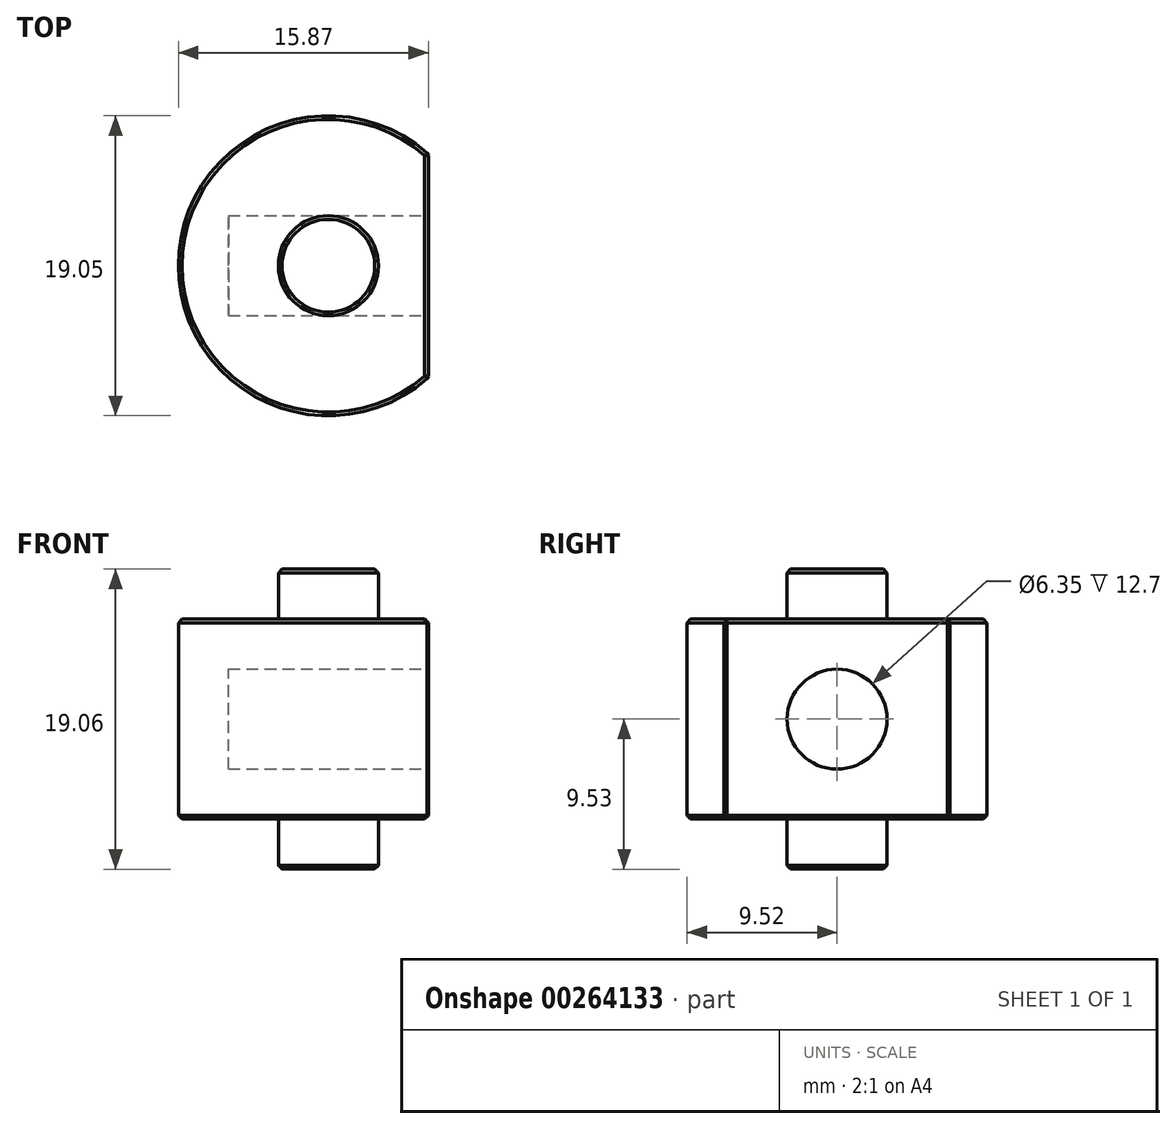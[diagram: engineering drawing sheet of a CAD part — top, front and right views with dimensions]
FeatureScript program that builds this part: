
annotation { "Feature Type Name" : "Feature", "Feature Type Description" : "" }
export const myFeature = defineFeature(function(context is Context, id is Id, definition is map)
    precondition{}
    {
        {
            var Q0;
            Q0=qCreatedBy(makeId("Top.planeOp"),FACE);
            var sketch = newSketch(context, id + "F0", { "sketchPlane" : qUnion([Q0])});
            skCircle(sketch, "E0", {"center": v(0, 0) * mm, "radius": 9.53 * mm});
            skLineSegment(sketch, "E1", {"start": v(6.35, 7.1) * mm, "end": v(6.35, -7.1) * mm});
            skSolve(sketch);
        }
        {
            var Q0;
            {var subQ0=sQuery(id+"F0.wireOp",EDGE,"E1");Q0=makeQuery(id+"F0.imprint","IMPRINT",FACE,{"disambiguationData":[TD([[makeQuery(id+"F0.imprint","IMPRINT",EDGE,{"derivedFrom":subQ0}),-1.0]])]});}
            extrude(context, id + "F1", {"entities" : qUnion([Q0]), "depth" : 12.7 * mm});
        }
        {
            var Q0;
            Q0=makeQuery(id+"F1.opExtrude","CAP_FACE",FACE,{"disambiguationData":[OSD([sQuery(id+"F0.wireOp",EDGE,"E0")])],"isStart":false});
            var sketch = newSketch(context, id + "F2", { "sketchPlane" : qUnion([Q0])});
            skCircle(sketch, "E2", {"center": v(0, 0) * mm, "radius": 3.18 * mm});
            skSolve(sketch);
        }
        {
            var Q0;
            Q0 = qSketchRegion(id + "F2", true);
            extrude(context, id + "F3", {"entities" : qUnion([Q0]), "operationType" : NewBodyOperationType.ADD, "depth" : 3.17 * mm});
        }
        {
            var Q0;
            Q0=makeQuery(id+"F1.opExtrude","CAP_FACE",FACE,{"disambiguationData":[OSD([sQuery(id+"F0.wireOp",EDGE,"E0")])],"isStart":true});
            var sketch = newSketch(context, id + "F4", { "sketchPlane" : qUnion([Q0])});
            skCircle(sketch, "E3", {"center": v(0, 0) * mm, "radius": 3.18 * mm});
            skSolve(sketch);
        }
        {
            var Q0;
            Q0 = qSketchRegion(id + "F4", true);
            extrude(context, id + "F5", {"entities" : qUnion([Q0]), "operationType" : NewBodyOperationType.ADD, "depth" : 3.17 * mm});
        }
        {
            var Q0;
            Q0=makeQuery(id+"F3.opExtrude","CAP_EDGE",EDGE,{"disambiguationData":[OSD([sQuery(id+"F2.wireOp",EDGE,"E2")])],"isStart":false});
            var Q1;
            Q1=makeQuery(id+"F1.opExtrude","CAP_EDGE",EDGE,{"disambiguationData":[OSD([sQuery(id+"F0.wireOp",EDGE,"E0")])],"isStart":false});
            var Q2;
            Q2=makeQuery(id+"F1.opExtrude","CAP_EDGE",EDGE,{"disambiguationData":[OSD([sQuery(id+"F0.wireOp",EDGE,"E1")])],"isStart":false});
            var Q3;
            {var subQ0=sQuery(id+"F0.wireOp",EDGE,"E1");var subQ1=sQuery(id+"F0.wireOp",EDGE,"E0");Q3=makeQuery(id+"F1.opExtrude","SWEPT_EDGE",EDGE,{"disambiguationData":[OSD([subQ1,subQ0]),TDD([makeQuery(id+"F0.imprint","INTERSECT",VERTEX,{"disambiguationData":[OD(0.0)],"derivedFrom":[subQ1,subQ0]})])]});}
            var Q4;
            Q4=makeQuery(id+"F1.opExtrude","CAP_EDGE",EDGE,{"disambiguationData":[OSD([sQuery(id+"F0.wireOp",EDGE,"E1")])],"isStart":true});
            var Q5;
            {var subQ0=sQuery(id+"F0.wireOp",EDGE,"E1");var subQ1=sQuery(id+"F0.wireOp",EDGE,"E0");Q5=makeQuery(id+"F1.opExtrude","SWEPT_EDGE",EDGE,{"disambiguationData":[OSD([subQ1,subQ0]),TDD([makeQuery(id+"F0.imprint","INTERSECT",VERTEX,{"disambiguationData":[OD(1.0)],"derivedFrom":[subQ1,subQ0]})])]});}
            var Q6;
            Q6=makeQuery(id+"F1.opExtrude","CAP_EDGE",EDGE,{"disambiguationData":[OSD([sQuery(id+"F0.wireOp",EDGE,"E0")])],"isStart":true});
            var Q7;
            Q7=makeQuery(id+"F5.opExtrude","CAP_EDGE",EDGE,{"disambiguationData":[OSD([sQuery(id+"F4.wireOp",EDGE,"E3")])],"isStart":false});
            chamfer(context, id + "F6", {"entities" : qUnion([Q0, Q1, Q2, Q3, Q4, Q5, Q6, Q7]), "width" : 0.23 * mm, "tangentPropagation" : true});
        }
        {
            var Q0;
            Q0=makeQuery(id+"F1.opExtrude","SWEPT_FACE",FACE,{"disambiguationData":[OSD([sQuery(id+"F0.wireOp",EDGE,"E1")])]});
            var sketch = newSketch(context, id + "F7", { "sketchPlane" : qUnion([Q0])});
            skCircle(sketch, "E4", {"center": v(0, 6.35) * mm, "radius": 3.18 * mm});
            skSolve(sketch);
        }
        {
            var Q0;
            Q0 = qSketchRegion(id + "F7", true);
            extrude(context, id + "F8", {"entities" : qUnion([Q0]), "operationType" : NewBodyOperationType.REMOVE, "oppositeDirection" : true, "depth" : 12.7 * mm});
        }
    });
